# Revit family: Flushometer-Sloan-TruFlush-TRF_Series
name_source: partatom
category: Plumbing Fixtures
revit_build: Autodesk Revit 2014 (Build: 20130308_1515(x64)
units: mm (PartAtom-declared; Revit-internal decimal feet)

## types (10) — shared parameters
ADA Compliant = Yes
CW Connection = Yes
Connection Diameter = 2"
Default Elevation = 0"
Description = Concealed piston type, rough brass, manual, true flushometer for top inlet or rear inlet, wall hung or floor mount, wash down or siphon jet toilets.
HW Connection = No
Height = 5"
Manufacturer = Sloan
Operating Pressure = 10-100 psi (0.7-7 bars)
Price = Prices may vary. Please consult Manufacturer Representative for most up-to-date price list.
Product Documentation Link = https://specifications.sloan.com
Product Page URL = https://www.sloan.com
Supply C/L to Finished Wall (2" MIN, 3" MAX) = 2"
Type Comments = Specify 1.25" (31.75 mm), 1" (25.4 mm) or .75" (19.1mm). Available with NPT or BSP-G threads.
URL = http://www.sloan.com
Valve Inlet Size = 1-1/2” NPT (female) Inlet standard
Valve Outlet Size = 1-1/2” NPSM Outlet standard
Vent Connection = No
Waste Connection = No
Width = 5"

## per-type parameters (varying)
| type | Faceplate Material | Fixture Type | Flush Cycle | Material | Model | SKU |
| TRF 156-1.6 Metal | Metal-Sloan-Chrome | Closet | 1.6 gpf/6.0 Lpf | Metal-Sloan-Chrome | TRF 156-1.6 | 3400005 |
| TRF 156-1.28 Metal | Metal-Sloan-Chrome | Closet | 1.28 gpf/4.8 Lpf | Metal-Sloan-Chrome | TRF 156-1.28 | 3400006 |
| TRF 196-0.5 - Metal | Metal-Sloan-Chrome | Urinal | 0.5 gpf/1.9 Lpf | Metal-Sloan-Chrome | TRF 196-0.5 | 3410007 |
| TRF 196-0.25 Metal | Metal-Sloan-Chrome | Urinal | 0.25 gpf/1.0 Lpf | Metal-Sloan-Chrome | TRF 196-0.25 | 3410008 |
| TRF 196-0.125 Metal | Metal-Sloan-Chrome | Urinal | 0.125 gpf/0.5 Lpf | Metal-Sloan-Chrome | TRF 196-0.125 | 3410004 |
| TRF 156-1.28 Plastic | Plastic-Sloan-Chrome | Closet | 1.28 gpf/4.8 Lpf | Plastic-Sloan-Chrome | TRF 156-1.28 | 3400001 |
| TRF 156-1.6 Plastic | Plastic-Sloan-Chrome | Closet | 1.6 gpf/6.0 Lpf | Plastic-Sloan-Chrome | TRF 156-1.6 | 3400000 |
| TRF 196-0.125 Plastic | Plastic-Sloan-Chrome | Urinal | 0.125 gpf/0.5 Lpf | Plastic-Sloan-Chrome | TRF 196-0.125 | 3410009 |
| TRF 196-0.25 Plastic | Plastic-Sloan-Chrome | Urinal | 0.25 gpf/1.0 Lpf | Plastic-Sloan-Chrome | TRF 196-0.25 | 3410003 |
| TRF 196-0.5 Plastic | Plastic-Sloan-Chrome | Urinal | 0.5 gpf/1.9 Lpf | Plastic-Sloan-Chrome | TRF 196-0.5 | 3400002 |

## geometry (parser evidence)
native form markers: Sweep x1
no freeform markers — native parametric forms only
